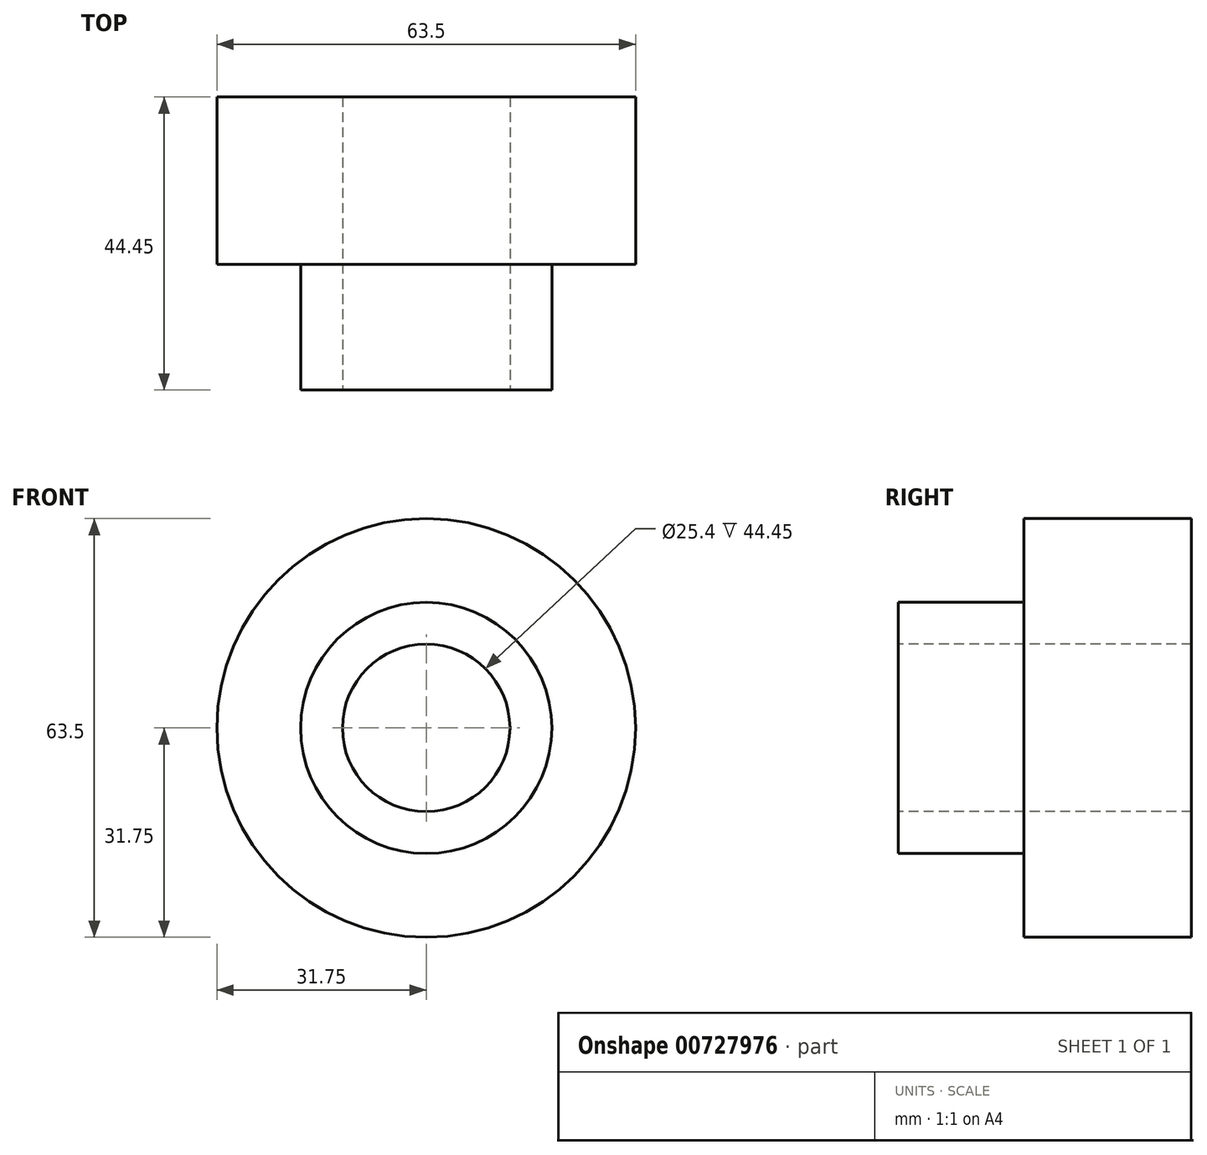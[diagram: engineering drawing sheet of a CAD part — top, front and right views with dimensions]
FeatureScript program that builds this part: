
annotation { "Feature Type Name" : "Feature", "Feature Type Description" : "" }
export const myFeature = defineFeature(function(context is Context, id is Id, definition is map)
    precondition{}
    {
        {
            var Q0;
            Q0=qCreatedBy(makeId("Front.planeOp"),FACE);
            var sketch = newSketch(context, id + "F0", { "sketchPlane" : qUnion([Q0])});
            skCircle(sketch, "E0", {"center": v(0, 0) * mm, "radius": 31.75 * mm});
            skSolve(sketch);
        }
        {
            var Q0;
            Q0=makeQuery(id+"F0.imprint","IMPRINT",FACE,{"disambiguationData":[TD([[makeQuery(id+"F0.imprint","IMPRINT",EDGE,{"derivedFrom":sQuery(id+"F0.wireOp",EDGE,"E0")}),1.0]])]});
            extrude(context, id + "F1", {"entities" : qUnion([Q0]), "depth" : 25.4 * mm, "offsetDistance" : 25.4 * mm});
        }
        {
            var Q0;
            Q0=makeQuery(id+"F1.opExtrude","CAP_FACE",FACE,{"disambiguationData":[OSD([sQuery(id+"F0.wireOp",EDGE,"E0")])],"isStart":false});
            var sketch = newSketch(context, id + "F2", { "sketchPlane" : qUnion([Q0])});
            skCircle(sketch, "E1", {"center": v(0, 0) * mm, "radius": 19.05 * mm});
            skSolve(sketch);
        }
        {
            var Q0;
            Q0=makeQuery(id+"F2.imprint","IMPRINT",FACE,{"disambiguationData":[TD([[makeQuery(id+"F2.imprint","IMPRINT",EDGE,{"derivedFrom":sQuery(id+"F2.wireOp",EDGE,"E1")}),1.0]])]});
            extrude(context, id + "F3", {"entities" : qUnion([Q0]), "operationType" : NewBodyOperationType.ADD, "depth" : 19.05 * mm, "offsetDistance" : 25.4 * mm});
        }
        {
            var Q0;
            Q0=makeQuery(id+"F3.opExtrude","CAP_FACE",FACE,{"disambiguationData":[OSD([sQuery(id+"F2.wireOp",EDGE,"E1")])],"isStart":false});
            var sketch = newSketch(context, id + "F4", { "sketchPlane" : qUnion([Q0])});
            skCircle(sketch, "E2", {"center": v(0, 0) * mm, "radius": 12.7 * mm});
            skSolve(sketch);
        }
        {
            var Q0;
            Q0=makeQuery(id+"F4.imprint","IMPRINT",FACE,{"disambiguationData":[TD([[makeQuery(id+"F4.imprint","IMPRINT",EDGE,{"derivedFrom":sQuery(id+"F4.wireOp",EDGE,"E2")}),1.0]])]});
            extrude(context, id + "F5", {"entities" : qUnion([Q0]), "operationType" : NewBodyOperationType.REMOVE, "endBound" : BoundingType.THROUGH_ALL, "oppositeDirection" : true, "depth" : 25.4 * mm, "offsetDistance" : 25.4 * mm});
        }
    });
